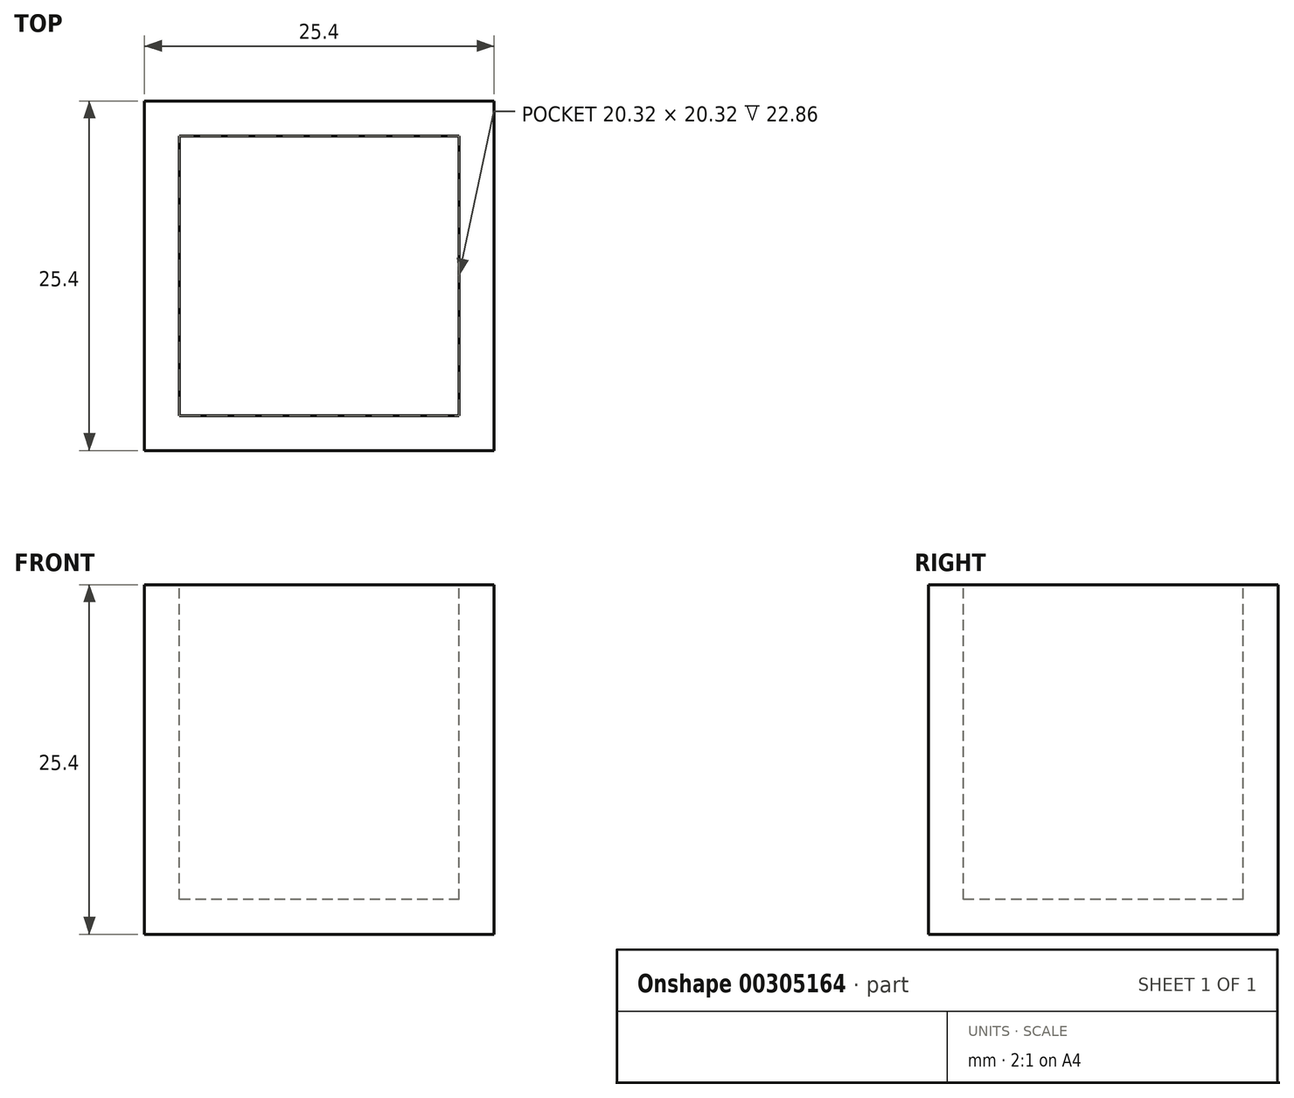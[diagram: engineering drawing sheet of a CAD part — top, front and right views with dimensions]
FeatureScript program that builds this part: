
annotation { "Feature Type Name" : "Feature", "Feature Type Description" : "" }
export const myFeature = defineFeature(function(context is Context, id is Id, definition is map)
    precondition{}
    {
        {
            var Q0;
            Q0=qCreatedBy(makeId("Front.planeOp"),FACE);
            var sketch = newSketch(context, id + "F0", { "sketchPlane" : qUnion([Q0])});
            skLineSegment(sketch, "E0.bottom", {"start": v(12.7, 12.7) * mm, "end": v(-12.7, 12.7) * mm});
            skLineSegment(sketch, "E0.top", {"start": v(12.7, -12.7) * mm, "end": v(-12.7, -12.7) * mm});
            skLineSegment(sketch, "E0.left", {"start": v(12.7, 12.7) * mm, "end": v(12.7, -12.7) * mm});
            skLineSegment(sketch, "E0.right", {"start": v(-12.7, 12.7) * mm, "end": v(-12.7, -12.7) * mm});
            skPoint(sketch, "E0.middle", {"position": v(0, 0) * mm});
            skSolve(sketch);
        }
        {
            var Q0;
            Q0=makeQuery(id+"F0.imprint","IMPRINT",FACE,{"disambiguationData":[TD([[makeQuery(id+"F0.imprint","IMPRINT",EDGE,{"derivedFrom":sQuery(id+"F0.wireOp",EDGE,"E0.bottom")}),1.0]])]});
            extrude(context, id + "F1", {"entities" : qUnion([Q0]), "depth" : 25.4 * mm});
        }
        {
            var Q0;
            Q0=makeQuery(id+"F1.opExtrude","SWEPT_FACE",FACE,{"disambiguationData":[OSD([sQuery(id+"F0.wireOp",EDGE,"E0.bottom")])]});
            var sketch = newSketch(context, id + "F2", { "sketchPlane" : qUnion([Q0])});
            skLineSegment(sketch, "E1.bottom", {"start": v(10.16, -2.54) * mm, "end": v(-10.16, -2.54) * mm});
            skLineSegment(sketch, "E1.top", {"start": v(10.16, -22.86) * mm, "end": v(-10.16, -22.86) * mm});
            skLineSegment(sketch, "E1.left", {"start": v(10.16, -2.54) * mm, "end": v(10.16, -22.86) * mm});
            skLineSegment(sketch, "E1.right", {"start": v(-10.16, -2.54) * mm, "end": v(-10.16, -22.86) * mm});
            skPoint(sketch, "E1.middle", {"position": v(0, -12.7) * mm});
            skSolve(sketch);
        }
        {
            var Q0;
            Q0 = qSketchRegion(id + "F2", true);
            extrude(context, id + "F3", {"entities" : qUnion([Q0]), "operationType" : NewBodyOperationType.REMOVE, "oppositeDirection" : true, "depth" : 22.86 * mm});
        }
    });
